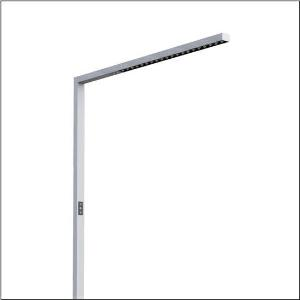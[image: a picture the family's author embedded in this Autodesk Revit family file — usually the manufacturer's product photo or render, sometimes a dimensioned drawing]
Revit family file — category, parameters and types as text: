
# Revit family: silica_r__31_floor_51my52fa4cs_7d3f
name_source: partatom
category: Lighting Fixtures
units: mm (PartAtom-declared; Revit-internal decimal feet)

## family parameters
Cut with Voids When Loaded = No
Host = Face
Light Source = No
Part Type = Normal
Room Calculation Point = No
Round Connector Dimension = Use Diameter
Shared = No

## types (1)
- Silica® 31 Floor (1 x LED, 10600 lm, 75 W, 4000K)
    Apparent Load = 75 VA
    CIE Flux Codes = 86 100 100 24 100
    Color Rendering = 80
    Color Temperature = 4000K
    Default Elevation = 1800 mm
    Description = Silica® 31 Floor, floorstanding luminaire, secondary optical cover: cover panel, of PMMA, light emission: direct/indirect distribution, primary light characteristic: symmetric, installation type: not mounted, LED, rated luminous flux: 10.600lm, luminous efficacy: 141lm/W, light colour: 840, colour temperature: 4000K, daylight-dependent control, with cable with plug, mains connection: 230V, AC, 50Hz, connection cable pre-assembled, rated input power: 75W, luminaire head, of aluminium, metallic grey (RAL 9006), length: 1.203mm, width: 52mm, supporting column, angular, of aluminium, metallic grey (RAL 9006), baseplate, of steel, metallic grey (RAL 9006), protection rating (complete): IP20, insulation class (complete): insulation class I (protective earthing), certification: CE, permissible operating ambient temperature: -20..+40°C, standard: EN 50419, packaging unit: 1 piece
    Height = 36 mm
    Lamp = 1 x LED
    Lamp Light Flux = 10600 lm
    Lamp Power = 75 W
    Lamp count = 1
    Length = 1203 mm
    Luminous efficacy = 141 lm/W
    Manufacturer = Siteco
    ModVariant = No
    Model = 51MY52FA4CS
    Mounting Place = Floor
    Mounting Type = Freestanding
    Number of Poles = 1
    OnlyDefault = Yes
    Power Factor = 1
    Product Name = Silica® 31 Floor
    Product group = floorstanding luminaire
    ProductGroupID = 1301
    Protection Class = Protection class I
    Protection Degree = IP 20
    RLX_Detail_Level = 1
    RLX_Emergency_Light_Flux = 0 lm
    RLX_Emergency_Type = 0
    RLX_Emergency_Type_DB = No
    RlxData = <blob elided: 19549 chars, md5=f86b55aa>
    Socket = socket
    Standby Power = 0 W
    System Light Flux = 10600 lm
    System Power = 75 W
    Type Comments = Product without accessories
    Type Image = l_1275303.jpg
    URL = http://relux.com
    VarID = ---
    Voltage = 0 V
    Weight = 0.00 kg
    Width = 52 mm  [stored 0.170604 ft]

note: [stored X ft] marks values corroborated as IEEE doubles in the binary element streams (Revit-internal decimal feet)

## geometry (parser evidence)
native form markers: Blend x4, Sweep x13
no freeform markers — native parametric forms only
